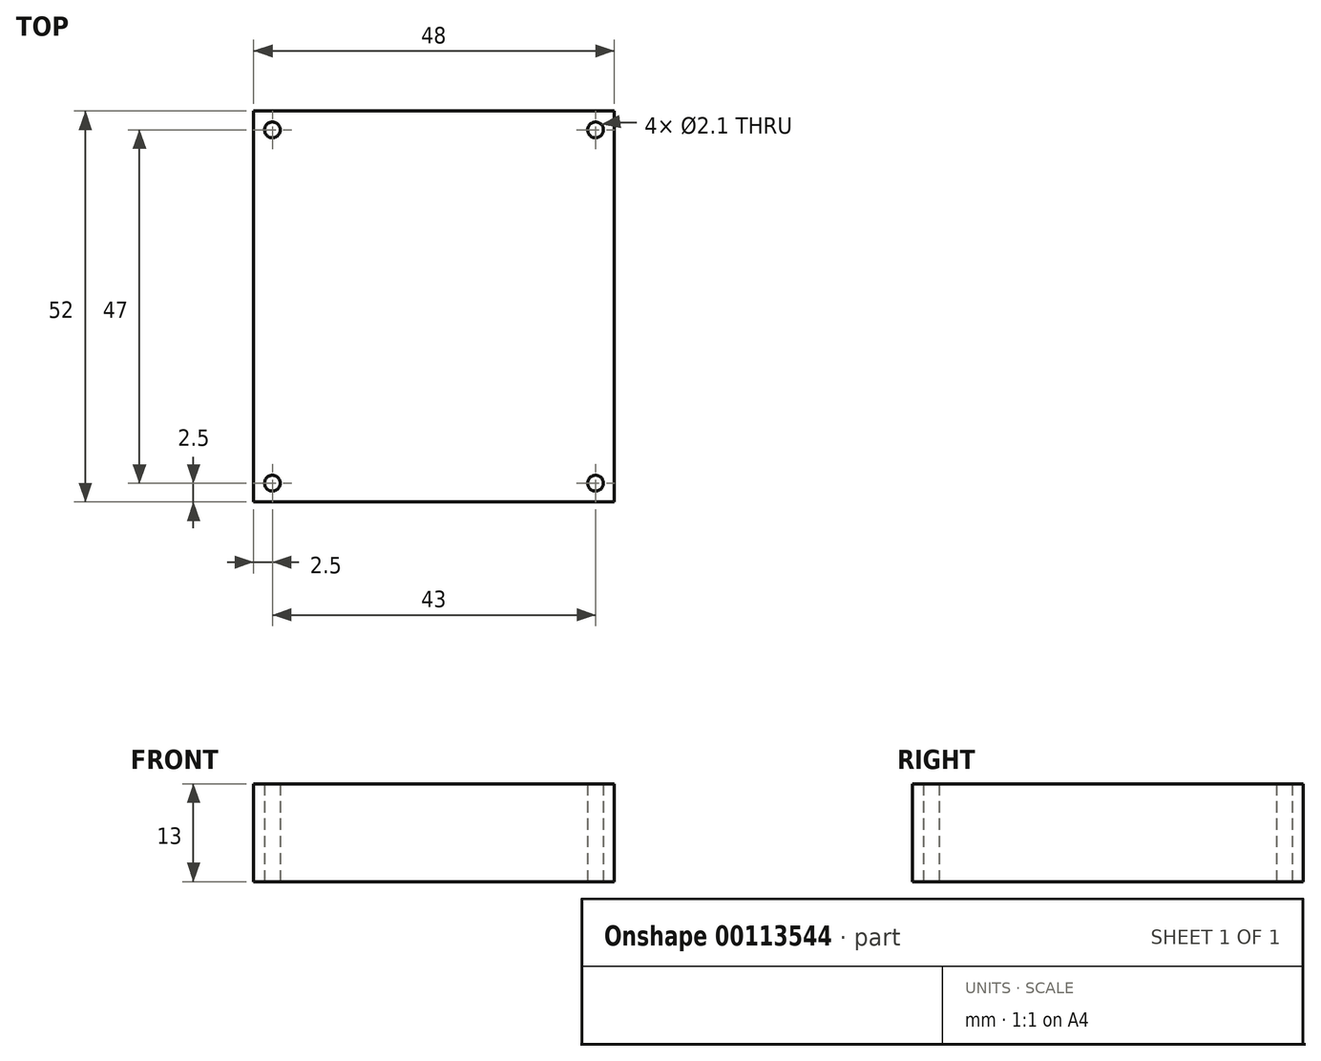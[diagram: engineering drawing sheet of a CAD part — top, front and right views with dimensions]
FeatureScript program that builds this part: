
annotation { "Feature Type Name" : "Feature", "Feature Type Description" : "" }
export const myFeature = defineFeature(function(context is Context, id is Id, definition is map)
    precondition{}
    {
        {
            var Q0;
            Q0=qCreatedBy(makeId("Top.planeOp"),FACE);
            var sketch = newSketch(context, id + "F0", { "sketchPlane" : qUnion([Q0])});
            skLineSegment(sketch, "E0.bottom", {"start": v(0, 0) * mm, "end": v(48, 0) * mm});
            skLineSegment(sketch, "E0.top", {"start": v(0, 52) * mm, "end": v(48, 52) * mm});
            skLineSegment(sketch, "E0.left", {"start": v(0, 0) * mm, "end": v(0, 52) * mm});
            skLineSegment(sketch, "E0.right", {"start": v(48, 0) * mm, "end": v(48, 52) * mm});
            skLineSegment(sketch, "E1", {"start": v(24, 52) * mm, "end": v(24, 0) * mm, "construction": true});
            skLineSegment(sketch, "E2", {"start": v(0, 26) * mm, "end": v(48, 26) * mm, "construction": true});
            skCircle(sketch, "E3", {"center": v(2.5, 49.5) * mm, "radius": 1.05 * mm});
            skCircle(sketch, "E4.MirrorC", {"center": v(45.5, 49.5) * mm, "radius": 1.05 * mm});
            skLineSegment(sketch, "E5.MirrorCS", {"start": v(48, 26) * mm, "end": v(0, 26) * mm, "construction": true});
            skCircle(sketch, "E6.MirrorC", {"center": v(2.5, 2.5) * mm, "radius": 1.05 * mm});
            skCircle(sketch, "E7.MirrorC", {"center": v(45.5, 2.5) * mm, "radius": 1.05 * mm});
            skSolve(sketch);
        }
        {
            var Q0;
            Q0=qSketchRegion(id+"F0",true);
            extrude(context, id + "F1", {"entities" : qUnion([Q0]), "depth" : 13 * mm});
        }
    });
